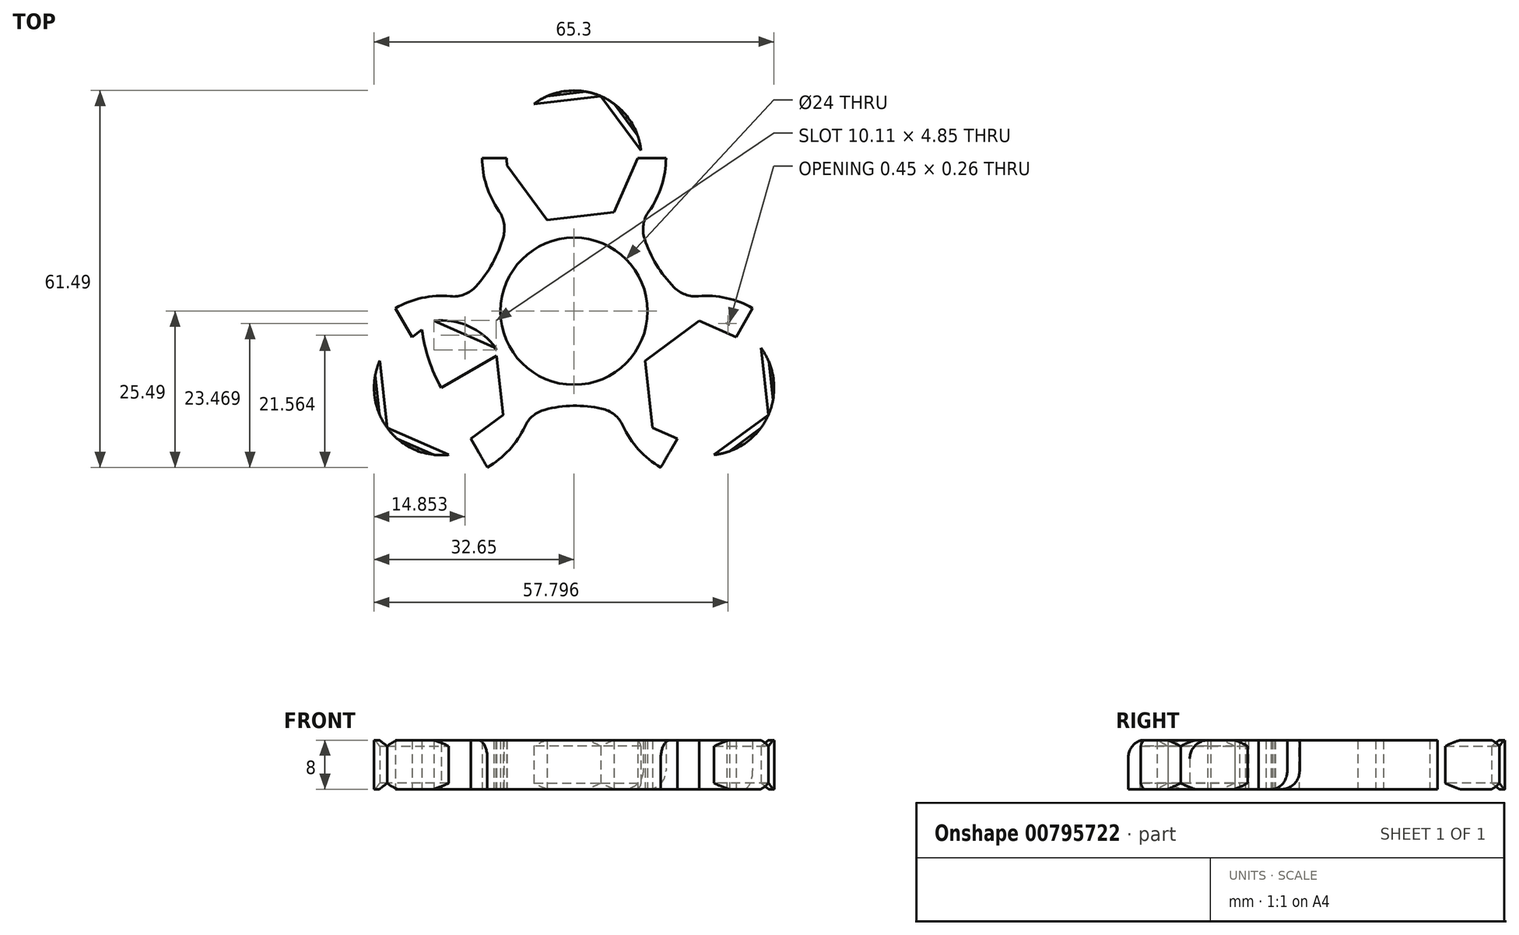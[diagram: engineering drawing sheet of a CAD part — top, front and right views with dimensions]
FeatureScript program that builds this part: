
annotation { "Feature Type Name" : "Feature", "Feature Type Description" : "" }
export const myFeature = defineFeature(function(context is Context, id is Id, definition is map)
    precondition{}
    {
        {
            var Q0;
            Q0=qCreatedBy(makeId("Top.planeOp"),FACE);
            var sketch = newSketch(context, id + "F0", { "sketchPlane" : qUnion([Q0])});
            skCircle(sketch, "E0.cCircle", {"center": v(0, 0) * mm, "radius": 25 * mm, "construction": true});
            skLineSegment(sketch, "E0.0", {"start": v(-43.3, 25) * mm, "end": v(43.3, 25) * mm});
            skLineSegment(sketch, "E0.1", {"start": v(43.3, 25) * mm, "end": v(0, -50) * mm});
            skLineSegment(sketch, "E0.2", {"start": v(-10.83, -31.25) * mm, "end": v(-43.3, 25) * mm});
            skPoint(sketch, "E0.0.midPoint", {"position": v(0, 25) * mm});
            skCircle(sketch, "E1", {"center": v(0, 0) * mm, "radius": 25 * mm});
            skLineSegment(sketch, "E2", {"start": v(0, 0) * mm, "end": v(-21.65, -12.5) * mm});
            skLineSegment(sketch, "E3", {"start": v(0, 0) * mm, "end": v(0, 25) * mm});
            skLineSegment(sketch, "E4", {"start": v(0, 0) * mm, "end": v(21.65, -12.5) * mm});
            skLineSegment(sketch, "E5", {"start": v(21.65, -12.5) * mm, "end": v(43.3, 25) * mm});
            skLineSegment(sketch, "E6", {"start": v(0, 25) * mm, "end": v(-43.3, 25) * mm});
            skLineSegment(sketch, "E7", {"start": v(-21.65, -12.5) * mm, "end": v(-43.3, 25) * mm});
            skLineSegment(sketch, "E8", {"start": v(-21.65, -12.5) * mm, "end": v(0, -50) * mm});
            skLineSegment(sketch, "E9", {"start": v(0, -50) * mm, "end": v(21.65, -12.5) * mm});
            skLineSegment(sketch, "E10", {"start": v(0, 25) * mm, "end": v(43.3, 25) * mm});
            skLineSegment(sketch, "E11", {"start": v(0, 25) * mm, "end": v(21.65, 25) * mm});
            skLineSegment(sketch, "E12", {"start": v(0, 25) * mm, "end": v(-21.65, 25) * mm});
            skLineSegment(sketch, "E13", {"start": v(-32.48, 6.25) * mm, "end": v(-43.3, 25) * mm});
            skLineSegment(sketch, "E14", {"start": v(-10.83, -31.25) * mm, "end": v(-21.65, -12.5) * mm});
            skLineSegment(sketch, "E15", {"start": v(21.65, -12.5) * mm, "end": v(32.48, 6.25) * mm});
            skLineSegment(sketch, "E16", {"start": v(32.48, 6.25) * mm, "end": v(27.06, -3.12) * mm});
            skLineSegment(sketch, "E17", {"start": v(21.65, 25) * mm, "end": v(10.83, 25) * mm});
            skLineSegment(sketch, "E18", {"start": v(-21.65, -12.5) * mm, "end": v(-16.24, -21.87) * mm});
            skArc(sketch, "E19", {"start": v(-16.24, -21.88) * mm, "mid": v(-12.28, -7.09) * mm, "end": v(-27.06, -3.12) * mm});
            skLineSegment(sketch, "E20", {"start": v(-16.24, -21.87) * mm, "end": v(-14.1, -20.64) * mm});
            skLineSegment(sketch, "E21", {"start": v(16.24, -21.87) * mm, "end": v(0, -12.5) * mm});
            skLineSegment(sketch, "E22", {"start": v(-16.24, -21.88) * mm, "end": v(0, -12.5) * mm});
            skLineSegment(sketch, "E23", {"start": v(-27.06, -3.12) * mm, "end": v(-10.83, 6.25) * mm});
            skLineSegment(sketch, "E24", {"start": v(-10.83, 25) * mm, "end": v(-10.83, 6.25) * mm});
            skLineSegment(sketch, "E25", {"start": v(10.83, 25) * mm, "end": v(10.83, 6.25) * mm});
            skLineSegment(sketch, "E26", {"start": v(27.06, -3.12) * mm, "end": v(10.83, 6.25) * mm});
            skCircle(sketch, "E27", {"center": v(-21.65, -12.5) * mm, "radius": 15 * mm});
            skCircle(sketch, "E28", {"center": v(0, 25) * mm, "radius": 15 * mm});
            skCircle(sketch, "E29", {"center": v(21.65, -12.5) * mm, "radius": 15 * mm});
            skCircle(sketch, "E30", {"center": v(0, 0) * mm, "radius": 12 * mm});
            skCircle(sketch, "E31", {"center": v(0, 25) * mm, "radius": 11 * mm});
            skCircle(sketch, "E32", {"center": v(-21.65, -12.5) * mm, "radius": 11 * mm});
            skCircle(sketch, "E33", {"center": v(21.65, -12.5) * mm, "radius": 11 * mm});
            skCircle(sketch, "E34.cCircle", {"center": v(21.65, -12.5) * mm, "radius": 11 * mm, "construction": true});
            skLineSegment(sketch, "E34.0", {"start": v(22.85, -23.43) * mm, "end": v(12.78, -19) * mm});
            skLineSegment(sketch, "E34.1", {"start": v(12.78, -19) * mm, "end": v(11.58, -8.07) * mm});
            skLineSegment(sketch, "E34.2", {"start": v(11.58, -8.07) * mm, "end": v(20.45, -1.57) * mm});
            skLineSegment(sketch, "E34.3", {"start": v(20.45, -1.57) * mm, "end": v(30.52, -6) * mm});
            skLineSegment(sketch, "E34.4", {"start": v(30.52, -6) * mm, "end": v(31.72, -16.93) * mm});
            skLineSegment(sketch, "E34.5", {"start": v(31.72, -16.93) * mm, "end": v(22.85, -23.43) * mm});
            skCircle(sketch, "E35.cCircle", {"center": v(-21.65, -12.5) * mm, "radius": 11 * mm, "construction": true});
            skLineSegment(sketch, "E35.0", {"start": v(-20.45, -23.43) * mm, "end": v(-30.52, -19) * mm});
            skLineSegment(sketch, "E35.1", {"start": v(-30.52, -19) * mm, "end": v(-31.72, -8.07) * mm});
            skLineSegment(sketch, "E35.2", {"start": v(-31.72, -8.07) * mm, "end": v(-22.85, -1.57) * mm});
            skLineSegment(sketch, "E35.3", {"start": v(-22.85, -1.57) * mm, "end": v(-12.78, -6) * mm});
            skLineSegment(sketch, "E35.4", {"start": v(-12.78, -6) * mm, "end": v(-11.58, -16.93) * mm});
            skLineSegment(sketch, "E35.5", {"start": v(-11.58, -16.93) * mm, "end": v(-20.45, -23.43) * mm});
            skCircle(sketch, "E36.cCircle", {"center": v(0, 25) * mm, "radius": 11 * mm, "construction": true});
            skLineSegment(sketch, "E36.0", {"start": v(-4.38, 14.9) * mm, "end": v(-10.93, 23.75) * mm});
            skLineSegment(sketch, "E36.1", {"start": v(-10.93, 23.75) * mm, "end": v(-6.55, 33.84) * mm});
            skLineSegment(sketch, "E36.2", {"start": v(-6.55, 33.84) * mm, "end": v(4.38, 35.1) * mm});
            skLineSegment(sketch, "E36.3", {"start": v(4.38, 35.1) * mm, "end": v(10.93, 26.25) * mm});
            skLineSegment(sketch, "E36.4", {"start": v(10.93, 26.25) * mm, "end": v(6.55, 16.16) * mm});
            skLineSegment(sketch, "E36.5", {"start": v(6.55, 16.16) * mm, "end": v(-4.38, 14.9) * mm});
            skSolve(sketch);
        }
        {
            var Q0;
            {var subQ0=sQuery(id+"F0.wireOp",EDGE,"E29");var subQ1=sQuery(id+"F0.wireOp",EDGE,"E9");var subQ2=makeQuery(id+"F0.imprint","INTERSECT",VERTEX,{"derivedFrom":[subQ1,subQ0]});Q0=makeQuery(id+"F0.imprint","IMPRINT",FACE,{"disambiguationData":[TD([[makeQuery(id+"F0.imprint","IMPRINT",EDGE,{"disambiguationData":[TD([[subQ2,-1.0]])],"derivedFrom":subQ1}),-1.0]])]});}
            var Q1;
            {var subQ0=sQuery(id+"F0.wireOp",EDGE,"E34.4");Q1=makeQuery(id+"F0.imprint","IMPRINT",FACE,{"disambiguationData":[TD([[makeQuery(id+"F0.imprint","IMPRINT",EDGE,{"derivedFrom":subQ0}),1.0]])]});}
            var Q2;
            {var subQ0=sQuery(id+"F0.wireOp",EDGE,"E34.5");Q2=makeQuery(id+"F0.imprint","IMPRINT",FACE,{"disambiguationData":[TD([[makeQuery(id+"F0.imprint","IMPRINT",EDGE,{"derivedFrom":subQ0}),1.0]])]});}
            var Q3;
            {var subQ0=sQuery(id+"F0.wireOp",EDGE,"E9");var subQ1=makeQuery(id+"F0.imprint","INTERSECT",VERTEX,{"derivedFrom":[subQ0,sQuery(id+"F0.wireOp",EDGE,"E21")]});Q3=makeQuery(id+"F0.imprint","IMPRINT",FACE,{"disambiguationData":[TD([[makeQuery(id+"F0.imprint","IMPRINT",EDGE,{"disambiguationData":[TD([[subQ1,1.0]])],"derivedFrom":subQ0}),-1.0]])]});}
            var Q4;
            {var subQ3=sQuery(id+"F0.wireOp",EDGE,"E33");var subQ5=sQuery(id+"F0.wireOp",EDGE,"E1");var subQ6=makeQuery(id+"F0.imprint","INTERSECT",VERTEX,{"disambiguationData":[OD(0.0)],"derivedFrom":[subQ5,subQ3]});Q4=makeQuery(id+"F0.imprint","IMPRINT",FACE,{"disambiguationData":[TD([[makeQuery(id+"F0.imprint","IMPRINT",EDGE,{"disambiguationData":[TD([[subQ6,-1.0]])],"derivedFrom":subQ5}),-1.0]])]});}
            var Q5;
            {var subQ0=sQuery(id+"F0.wireOp",EDGE,"E21");var subQ1=sQuery(id+"F0.wireOp",EDGE,"E9");var subQ2=makeQuery(id+"F0.imprint","INTERSECT",VERTEX,{"derivedFrom":[subQ1,subQ0]});Q5=makeQuery(id+"F0.imprint","IMPRINT",FACE,{"disambiguationData":[TD([[makeQuery(id+"F0.imprint","IMPRINT",EDGE,{"disambiguationData":[TD([[subQ2,1.0]])],"derivedFrom":subQ1}),1.0]])]});}
            var Q6;
            {var subQ0=sQuery(id+"F0.wireOp",EDGE,"E33");var subQ1=sQuery(id+"F0.wireOp",EDGE,"E1");var subQ2=makeQuery(id+"F0.imprint","INTERSECT",VERTEX,{"disambiguationData":[OD(0.0)],"derivedFrom":[subQ1,subQ0]});Q6=makeQuery(id+"F0.imprint","IMPRINT",FACE,{"disambiguationData":[TD([[makeQuery(id+"F0.imprint","IMPRINT",EDGE,{"disambiguationData":[TD([[subQ2,-1.0]])],"derivedFrom":subQ1}),1.0]])]});}
            var Q7;
            {var subQ0=sQuery(id+"F0.wireOp",EDGE,"E21");var subQ1=sQuery(id+"F0.wireOp",EDGE,"E1");var subQ2=makeQuery(id+"F0.imprint","INTERSECT",VERTEX,{"derivedFrom":[subQ1,subQ0]});Q7=makeQuery(id+"F0.imprint","IMPRINT",FACE,{"disambiguationData":[TD([[makeQuery(id+"F0.imprint","IMPRINT",EDGE,{"disambiguationData":[TD([[subQ2,-1.0]])],"derivedFrom":subQ1}),-1.0]])]});}
            var Q8;
            {var subQ0=sQuery(id+"F0.wireOp",EDGE,"E29");var subQ5=sQuery(id+"F0.wireOp",EDGE,"E1");var subQ6=makeQuery(id+"F0.imprint","INTERSECT",VERTEX,{"disambiguationData":[OD(1.0)],"derivedFrom":[subQ5,subQ0]});Q8=makeQuery(id+"F0.imprint","IMPRINT",FACE,{"disambiguationData":[TD([[makeQuery(id+"F0.imprint","IMPRINT",EDGE,{"disambiguationData":[TD([[subQ6,-1.0]])],"derivedFrom":subQ5}),-1.0]])]});}
            var Q9;
            {var subQ0=sQuery(id+"F0.wireOp",EDGE,"E29");var subQ1=sQuery(id+"F0.wireOp",EDGE,"E1");var subQ2=makeQuery(id+"F0.imprint","INTERSECT",VERTEX,{"disambiguationData":[OD(1.0)],"derivedFrom":[subQ1,subQ0]});Q9=makeQuery(id+"F0.imprint","IMPRINT",FACE,{"disambiguationData":[TD([[makeQuery(id+"F0.imprint","IMPRINT",EDGE,{"disambiguationData":[TD([[subQ2,-1.0]])],"derivedFrom":subQ1}),1.0]])]});}
            var Q10;
            {var subQ1=sQuery(id+"F0.wireOp",EDGE,"E21");var subQ10=sQuery(id+"F0.wireOp",EDGE,"E1");var subQ11=makeQuery(id+"F0.imprint","INTERSECT",VERTEX,{"derivedFrom":[subQ10,subQ1]});Q10=makeQuery(id+"F0.imprint","IMPRINT",FACE,{"disambiguationData":[TD([[makeQuery(id+"F0.imprint","IMPRINT",EDGE,{"disambiguationData":[TD([[subQ11,-1.0]])],"derivedFrom":subQ10}),1.0]])]});}
            var Q11;
            {var subQ0=sQuery(id+"F0.wireOp",EDGE,"E34.1");Q11=makeQuery(id+"F0.imprint","IMPRINT",FACE,{"disambiguationData":[TD([[makeQuery(id+"F0.imprint","IMPRINT",EDGE,{"derivedFrom":subQ0}),1.0]])]});}
            var Q12;
            {var subQ0=sQuery(id+"F0.wireOp",EDGE,"E33");var subQ1=sQuery(id+"F0.wireOp",EDGE,"E4");var subQ2=makeQuery(id+"F0.imprint","INTERSECT",VERTEX,{"derivedFrom":[subQ1,subQ0]});Q12=makeQuery(id+"F0.imprint","IMPRINT",FACE,{"disambiguationData":[TD([[makeQuery(id+"F0.imprint","IMPRINT",EDGE,{"disambiguationData":[TD([[subQ2,-1.0]])],"derivedFrom":subQ1}),1.0]])]});}
            var Q13;
            {var subQ0=sQuery(id+"F0.wireOp",EDGE,"E33");var subQ1=sQuery(id+"F0.wireOp",EDGE,"E4");var subQ2=makeQuery(id+"F0.imprint","INTERSECT",VERTEX,{"derivedFrom":[subQ1,subQ0]});Q13=makeQuery(id+"F0.imprint","IMPRINT",FACE,{"disambiguationData":[TD([[makeQuery(id+"F0.imprint","IMPRINT",EDGE,{"disambiguationData":[TD([[subQ2,-1.0]])],"derivedFrom":subQ1}),-1.0]])]});}
            var Q14;
            {var subQ0=sQuery(id+"F0.wireOp",EDGE,"E34.3");var subQ1=sQuery(id+"F0.wireOp",EDGE,"E1");var subQ2=makeQuery(id+"F0.imprint","INTERSECT",VERTEX,{"derivedFrom":[subQ1,subQ0]});Q14=makeQuery(id+"F0.imprint","IMPRINT",FACE,{"disambiguationData":[TD([[makeQuery(id+"F0.imprint","IMPRINT",EDGE,{"disambiguationData":[TD([[subQ2,-1.0]])],"derivedFrom":subQ1}),1.0]])]});}
            var Q15;
            {var subQ1=sQuery(id+"F0.wireOp",EDGE,"E1");var subQ5=sQuery(id+"F0.wireOp",EDGE,"E34.3");var subQ6=makeQuery(id+"F0.imprint","INTERSECT",VERTEX,{"derivedFrom":[subQ1,subQ5]});Q15=makeQuery(id+"F0.imprint","IMPRINT",FACE,{"disambiguationData":[TD([[makeQuery(id+"F0.imprint","IMPRINT",EDGE,{"disambiguationData":[TD([[subQ6,-1.0]])],"derivedFrom":subQ1}),-1.0]])]});}
            var Q16;
            {var subQ1=sQuery(id+"F0.wireOp",EDGE,"E15");var subQ3=sQuery(id+"F0.wireOp",EDGE,"E34.3");var subQ4=makeQuery(id+"F0.imprint","INTERSECT",VERTEX,{"derivedFrom":[subQ1,subQ3]});Q16=makeQuery(id+"F0.imprint","IMPRINT",FACE,{"disambiguationData":[TD([[makeQuery(id+"F0.imprint","IMPRINT",EDGE,{"disambiguationData":[TD([[subQ4,-1.0]])],"derivedFrom":subQ1}),-1.0]])]});}
            var Q17;
            {var subQ1=sQuery(id+"F0.wireOp",EDGE,"E16");var subQ3=sQuery(id+"F0.wireOp",EDGE,"E33");var subQ4=makeQuery(id+"F0.imprint","INTERSECT",VERTEX,{"derivedFrom":[subQ1,subQ3]});Q17=makeQuery(id+"F0.imprint","IMPRINT",FACE,{"disambiguationData":[TD([[makeQuery(id+"F0.imprint","IMPRINT",EDGE,{"disambiguationData":[TD([[subQ4,-1.0]])],"derivedFrom":subQ3}),1.0]])]});}
            var Q18;
            {var subQ0=sQuery(id+"F0.wireOp",EDGE,"E29");var subQ3=sQuery(id+"F0.wireOp",EDGE,"E1");var subQ4=makeQuery(id+"F0.imprint","INTERSECT",VERTEX,{"disambiguationData":[OD(0.0)],"derivedFrom":[subQ3,subQ0]});Q18=makeQuery(id+"F0.imprint","IMPRINT",FACE,{"disambiguationData":[TD([[makeQuery(id+"F0.imprint","IMPRINT",EDGE,{"disambiguationData":[TD([[subQ4,1.0]])],"derivedFrom":subQ3}),-1.0]])]});}
            var Q19;
            {var subQ5=sQuery(id+"F0.wireOp",EDGE,"E1");var subQ9=sQuery(id+"F0.wireOp",EDGE,"E33");var subQ11=makeQuery(id+"F0.imprint","INTERSECT",VERTEX,{"disambiguationData":[OD(1.0)],"derivedFrom":[subQ5,subQ9]});Q19=makeQuery(id+"F0.imprint","IMPRINT",FACE,{"disambiguationData":[TD([[makeQuery(id+"F0.imprint","IMPRINT",EDGE,{"disambiguationData":[TD([[subQ11,-1.0]])],"derivedFrom":subQ5}),1.0]])]});}
            var Q20;
            {var subQ0=sQuery(id+"F0.wireOp",EDGE,"E29");var subQ1=sQuery(id+"F0.wireOp",EDGE,"E1");var subQ2=makeQuery(id+"F0.imprint","INTERSECT",VERTEX,{"disambiguationData":[OD(0.0)],"derivedFrom":[subQ1,subQ0]});Q20=makeQuery(id+"F0.imprint","IMPRINT",FACE,{"disambiguationData":[TD([[makeQuery(id+"F0.imprint","IMPRINT",EDGE,{"disambiguationData":[TD([[subQ2,1.0]])],"derivedFrom":subQ1}),1.0]])]});}
            var Q21;
            {var subQ1=sQuery(id+"F0.wireOp",EDGE,"E21");var subQ6=sQuery(id+"F0.wireOp",EDGE,"E22");var subQ9=makeQuery(id+"F0.imprint","INTERSECT",VERTEX,{"derivedFrom":[subQ1,subQ6]});Q21=makeQuery(id+"F0.imprint","IMPRINT",FACE,{"disambiguationData":[TD([[makeQuery(id+"F0.imprint","IMPRINT",EDGE,{"disambiguationData":[TD([[subQ9,1.0]])],"derivedFrom":subQ1}),-1.0]])]});}
            var Q22;
            {var subQ0=sQuery(id+"F0.wireOp",EDGE,"E22");var subQ1=sQuery(id+"F0.wireOp",EDGE,"E1");var subQ2=makeQuery(id+"F0.imprint","INTERSECT",VERTEX,{"derivedFrom":[subQ1,subQ0]});Q22=makeQuery(id+"F0.imprint","IMPRINT",FACE,{"disambiguationData":[TD([[makeQuery(id+"F0.imprint","IMPRINT",EDGE,{"disambiguationData":[TD([[subQ2,-1.0]])],"derivedFrom":subQ1}),1.0]])]});}
            var Q23;
            {var subQ3=sQuery(id+"F0.wireOp",EDGE,"E1");var subQ5=sQuery(id+"F0.wireOp",EDGE,"E22");var subQ6=makeQuery(id+"F0.imprint","INTERSECT",VERTEX,{"derivedFrom":[subQ3,subQ5]});Q23=makeQuery(id+"F0.imprint","IMPRINT",FACE,{"disambiguationData":[TD([[makeQuery(id+"F0.imprint","IMPRINT",EDGE,{"disambiguationData":[TD([[subQ6,-1.0]])],"derivedFrom":subQ3}),-1.0]])]});}
            var Q24;
            {var subQ0=sQuery(id+"F0.wireOp",EDGE,"E27");var subQ1=sQuery(id+"F0.wireOp",EDGE,"E7");var subQ2=makeQuery(id+"F0.imprint","INTERSECT",VERTEX,{"derivedFrom":[subQ1,subQ0]});Q24=makeQuery(id+"F0.imprint","IMPRINT",FACE,{"disambiguationData":[TD([[makeQuery(id+"F0.imprint","IMPRINT",EDGE,{"disambiguationData":[TD([[subQ2,1.0]])],"derivedFrom":subQ1}),1.0]])]});}
            var Q25;
            {var subQ1=sQuery(id+"F0.wireOp",EDGE,"E1");var subQ5=sQuery(id+"F0.wireOp",EDGE,"E27");var subQ8=makeQuery(id+"F0.imprint","INTERSECT",VERTEX,{"disambiguationData":[OD(0.0)],"derivedFrom":[subQ1,subQ5]});Q25=makeQuery(id+"F0.imprint","IMPRINT",FACE,{"disambiguationData":[TD([[makeQuery(id+"F0.imprint","IMPRINT",EDGE,{"disambiguationData":[TD([[subQ8,-1.0]])],"derivedFrom":subQ1}),-1.0]])]});}
            var Q26;
            {var subQ0=sQuery(id+"F0.wireOp",EDGE,"E27");var subQ1=sQuery(id+"F0.wireOp",EDGE,"E1");var subQ2=makeQuery(id+"F0.imprint","INTERSECT",VERTEX,{"disambiguationData":[OD(0.0)],"derivedFrom":[subQ1,subQ0]});Q26=makeQuery(id+"F0.imprint","IMPRINT",FACE,{"disambiguationData":[TD([[makeQuery(id+"F0.imprint","IMPRINT",EDGE,{"disambiguationData":[TD([[subQ2,-1.0]])],"derivedFrom":subQ1}),1.0]])]});}
            var Q27;
            {var subQ1=sQuery(id+"F0.wireOp",EDGE,"E23");var subQ5=sQuery(id+"F0.wireOp",EDGE,"E1");var subQ6=makeQuery(id+"F0.imprint","INTERSECT",VERTEX,{"derivedFrom":[subQ5,subQ1]});Q27=makeQuery(id+"F0.imprint","IMPRINT",FACE,{"disambiguationData":[TD([[makeQuery(id+"F0.imprint","IMPRINT",EDGE,{"disambiguationData":[TD([[subQ6,-1.0]])],"derivedFrom":subQ5}),1.0]])]});}
            var Q28;
            {var subQ5=sQuery(id+"F0.wireOp",EDGE,"E1");var subQ9=sQuery(id+"F0.wireOp",EDGE,"E32");var subQ11=makeQuery(id+"F0.imprint","INTERSECT",VERTEX,{"disambiguationData":[OD(1.0)],"derivedFrom":[subQ5,subQ9]});Q28=makeQuery(id+"F0.imprint","IMPRINT",FACE,{"disambiguationData":[TD([[makeQuery(id+"F0.imprint","IMPRINT",EDGE,{"disambiguationData":[TD([[subQ11,-1.0]])],"derivedFrom":subQ5}),1.0]])]});}
            var Q29;
            {var subQ1=sQuery(id+"F0.wireOp",EDGE,"E7");var subQ3=sQuery(id+"F0.wireOp",EDGE,"E32");var subQ4=makeQuery(id+"F0.imprint","INTERSECT",VERTEX,{"derivedFrom":[subQ1,subQ3]});Q29=makeQuery(id+"F0.imprint","IMPRINT",FACE,{"disambiguationData":[TD([[makeQuery(id+"F0.imprint","IMPRINT",EDGE,{"disambiguationData":[TD([[subQ4,1.0]])],"derivedFrom":subQ3}),1.0]])]});}
            var Q30;
            {var subQ0=sQuery(id+"F0.wireOp",EDGE,"E23");var subQ1=sQuery(id+"F0.wireOp",EDGE,"E1");var subQ2=makeQuery(id+"F0.imprint","INTERSECT",VERTEX,{"derivedFrom":[subQ1,subQ0]});Q30=makeQuery(id+"F0.imprint","IMPRINT",FACE,{"disambiguationData":[TD([[makeQuery(id+"F0.imprint","IMPRINT",EDGE,{"disambiguationData":[TD([[subQ2,-1.0]])],"derivedFrom":subQ1}),-1.0]])]});}
            var Q31;
            {var subQ0=sQuery(id+"F0.wireOp",EDGE,"E32");var subQ1=sQuery(id+"F0.wireOp",EDGE,"E1");var subQ2=makeQuery(id+"F0.imprint","INTERSECT",VERTEX,{"disambiguationData":[OD(0.0)],"derivedFrom":[subQ1,subQ0]});Q31=makeQuery(id+"F0.imprint","IMPRINT",FACE,{"disambiguationData":[TD([[makeQuery(id+"F0.imprint","IMPRINT",EDGE,{"disambiguationData":[TD([[subQ2,-1.0]])],"derivedFrom":subQ1}),-1.0]])]});}
            var Q32;
            {var subQ0=sQuery(id+"F0.wireOp",EDGE,"E32");var subQ1=sQuery(id+"F0.wireOp",EDGE,"E1");var subQ2=makeQuery(id+"F0.imprint","INTERSECT",VERTEX,{"disambiguationData":[OD(0.0)],"derivedFrom":[subQ1,subQ0]});Q32=makeQuery(id+"F0.imprint","IMPRINT",FACE,{"disambiguationData":[TD([[makeQuery(id+"F0.imprint","IMPRINT",EDGE,{"disambiguationData":[TD([[subQ2,-1.0]])],"derivedFrom":subQ1}),1.0]])]});}
            var Q33;
            {var subQ0=sQuery(id+"F0.wireOp",EDGE,"E35.3");var subQ1=sQuery(id+"F0.wireOp",EDGE,"E19");var subQ2=makeQuery(id+"F0.imprint","INTERSECT",VERTEX,{"disambiguationData":[OD(0.0)],"derivedFrom":[subQ1,subQ0]});Q33=makeQuery(id+"F0.imprint","IMPRINT",FACE,{"disambiguationData":[TD([[makeQuery(id+"F0.imprint","IMPRINT",EDGE,{"disambiguationData":[TD([[subQ2,-1.0]])],"derivedFrom":subQ1}),-1.0]])]});}
            var Q34;
            {var subQ0=sQuery(id+"F0.wireOp",EDGE,"E19");var subQ1=sQuery(id+"F0.wireOp",EDGE,"E1");var subQ2=makeQuery(id+"F0.imprint","INTERSECT",VERTEX,{"disambiguationData":[OD(0.0)],"derivedFrom":[subQ1,subQ0]});Q34=makeQuery(id+"F0.imprint","IMPRINT",FACE,{"disambiguationData":[TD([[makeQuery(id+"F0.imprint","IMPRINT",EDGE,{"disambiguationData":[TD([[subQ2,-1.0]])],"derivedFrom":subQ1}),-1.0]])]});}
            var Q35;
            {var subQ0=sQuery(id+"F0.wireOp",EDGE,"E19");var subQ1=sQuery(id+"F0.wireOp",EDGE,"E1");var subQ2=makeQuery(id+"F0.imprint","INTERSECT",VERTEX,{"disambiguationData":[OD(0.0)],"derivedFrom":[subQ1,subQ0]});Q35=makeQuery(id+"F0.imprint","IMPRINT",FACE,{"disambiguationData":[TD([[makeQuery(id+"F0.imprint","IMPRINT",EDGE,{"disambiguationData":[TD([[subQ2,-1.0]])],"derivedFrom":subQ1}),1.0]])]});}
            var Q36;
            {var subQ0=sQuery(id+"F0.wireOp",EDGE,"E7");var subQ2=sQuery(id+"F0.wireOp",EDGE,"E35.2");var subQ3=makeQuery(id+"F0.imprint","INTERSECT",VERTEX,{"derivedFrom":[subQ0,subQ2]});Q36=makeQuery(id+"F0.imprint","IMPRINT",FACE,{"disambiguationData":[TD([[makeQuery(id+"F0.imprint","IMPRINT",EDGE,{"disambiguationData":[TD([[subQ3,-1.0]])],"derivedFrom":subQ0}),1.0]])]});}
            var Q37;
            {var subQ0=sQuery(id+"F0.wireOp",EDGE,"E35.1");Q37=makeQuery(id+"F0.imprint","IMPRINT",FACE,{"disambiguationData":[TD([[makeQuery(id+"F0.imprint","IMPRINT",EDGE,{"derivedFrom":subQ0}),1.0]])]});}
            var Q38;
            {var subQ0=sQuery(id+"F0.wireOp",EDGE,"E35.0");Q38=makeQuery(id+"F0.imprint","IMPRINT",FACE,{"disambiguationData":[TD([[makeQuery(id+"F0.imprint","IMPRINT",EDGE,{"derivedFrom":subQ0}),1.0]])]});}
            var Q39;
            {var subQ1=sQuery(id+"F0.wireOp",EDGE,"E14");var subQ3=sQuery(id+"F0.wireOp",EDGE,"E32");var subQ4=makeQuery(id+"F0.imprint","INTERSECT",VERTEX,{"derivedFrom":[subQ1,subQ3]});Q39=makeQuery(id+"F0.imprint","IMPRINT",FACE,{"disambiguationData":[TD([[makeQuery(id+"F0.imprint","IMPRINT",EDGE,{"disambiguationData":[TD([[subQ4,1.0]])],"derivedFrom":subQ3}),1.0]])]});}
            var Q40;
            {var subQ0=sQuery(id+"F0.wireOp",EDGE,"E19");var subQ1=sQuery(id+"F0.wireOp",EDGE,"E1");var subQ2=makeQuery(id+"F0.imprint","INTERSECT",VERTEX,{"disambiguationData":[OD(1.0)],"derivedFrom":[subQ1,subQ0]});Q40=makeQuery(id+"F0.imprint","IMPRINT",FACE,{"disambiguationData":[TD([[makeQuery(id+"F0.imprint","IMPRINT",EDGE,{"disambiguationData":[TD([[subQ2,-1.0]])],"derivedFrom":subQ1}),-1.0]])]});}
            var Q41;
            {var subQ1=sQuery(id+"F0.wireOp",EDGE,"E14");var subQ3=sQuery(id+"F0.wireOp",EDGE,"E32");var subQ4=makeQuery(id+"F0.imprint","INTERSECT",VERTEX,{"derivedFrom":[subQ1,subQ3]});Q41=makeQuery(id+"F0.imprint","IMPRINT",FACE,{"disambiguationData":[TD([[makeQuery(id+"F0.imprint","IMPRINT",EDGE,{"disambiguationData":[TD([[subQ4,-1.0]])],"derivedFrom":subQ3}),1.0]])]});}
            var Q42;
            {var subQ0=sQuery(id+"F0.wireOp",EDGE,"E35.5");var subQ1=sQuery(id+"F0.wireOp",EDGE,"E1");var subQ2=makeQuery(id+"F0.imprint","INTERSECT",VERTEX,{"derivedFrom":[subQ1,subQ0]});Q42=makeQuery(id+"F0.imprint","IMPRINT",FACE,{"disambiguationData":[TD([[makeQuery(id+"F0.imprint","IMPRINT",EDGE,{"disambiguationData":[TD([[subQ2,-1.0]])],"derivedFrom":subQ1}),-1.0]])]});}
            var Q43;
            {var subQ0=sQuery(id+"F0.wireOp",EDGE,"E32");var subQ1=sQuery(id+"F0.wireOp",EDGE,"E1");var subQ2=makeQuery(id+"F0.imprint","INTERSECT",VERTEX,{"disambiguationData":[OD(1.0)],"derivedFrom":[subQ1,subQ0]});Q43=makeQuery(id+"F0.imprint","IMPRINT",FACE,{"disambiguationData":[TD([[makeQuery(id+"F0.imprint","IMPRINT",EDGE,{"disambiguationData":[TD([[subQ2,-1.0]])],"derivedFrom":subQ1}),-1.0]])]});}
            var Q44;
            {var subQ0=sQuery(id+"F0.wireOp",EDGE,"E19");var subQ1=sQuery(id+"F0.wireOp",EDGE,"E1");var subQ2=makeQuery(id+"F0.imprint","INTERSECT",VERTEX,{"disambiguationData":[OD(1.0)],"derivedFrom":[subQ1,subQ0]});Q44=makeQuery(id+"F0.imprint","IMPRINT",FACE,{"disambiguationData":[TD([[makeQuery(id+"F0.imprint","IMPRINT",EDGE,{"disambiguationData":[TD([[subQ2,-1.0]])],"derivedFrom":subQ1}),1.0]])]});}
            var Q45;
            {var subQ0=sQuery(id+"F0.wireOp",EDGE,"E35.5");var subQ1=sQuery(id+"F0.wireOp",EDGE,"E1");var subQ2=makeQuery(id+"F0.imprint","INTERSECT",VERTEX,{"derivedFrom":[subQ1,subQ0]});Q45=makeQuery(id+"F0.imprint","IMPRINT",FACE,{"disambiguationData":[TD([[makeQuery(id+"F0.imprint","IMPRINT",EDGE,{"disambiguationData":[TD([[subQ2,-1.0]])],"derivedFrom":subQ1}),1.0]])]});}
            var Q46;
            {var subQ0=sQuery(id+"F0.wireOp",EDGE,"E32");var subQ1=sQuery(id+"F0.wireOp",EDGE,"E2");var subQ2=makeQuery(id+"F0.imprint","INTERSECT",VERTEX,{"derivedFrom":[subQ1,subQ0]});Q46=makeQuery(id+"F0.imprint","IMPRINT",FACE,{"disambiguationData":[TD([[makeQuery(id+"F0.imprint","IMPRINT",EDGE,{"disambiguationData":[TD([[subQ2,-1.0]])],"derivedFrom":subQ1}),1.0]])]});}
            var Q47;
            {var subQ0=sQuery(id+"F0.wireOp",EDGE,"E19");var subQ1=sQuery(id+"F0.wireOp",EDGE,"E2");var subQ2=makeQuery(id+"F0.imprint","INTERSECT",VERTEX,{"derivedFrom":[subQ1,subQ0]});Q47=makeQuery(id+"F0.imprint","IMPRINT",FACE,{"disambiguationData":[TD([[makeQuery(id+"F0.imprint","IMPRINT",EDGE,{"disambiguationData":[TD([[subQ2,-1.0]])],"derivedFrom":subQ1}),1.0]])]});}
            var Q48;
            {var subQ0=sQuery(id+"F0.wireOp",EDGE,"E19");var subQ1=sQuery(id+"F0.wireOp",EDGE,"E2");var subQ2=makeQuery(id+"F0.imprint","INTERSECT",VERTEX,{"derivedFrom":[subQ1,subQ0]});Q48=makeQuery(id+"F0.imprint","IMPRINT",FACE,{"disambiguationData":[TD([[makeQuery(id+"F0.imprint","IMPRINT",EDGE,{"disambiguationData":[TD([[subQ2,-1.0]])],"derivedFrom":subQ1}),-1.0]])]});}
            var Q49;
            {var subQ0=sQuery(id+"F0.wireOp",EDGE,"E32");var subQ1=sQuery(id+"F0.wireOp",EDGE,"E2");var subQ2=makeQuery(id+"F0.imprint","INTERSECT",VERTEX,{"derivedFrom":[subQ1,subQ0]});Q49=makeQuery(id+"F0.imprint","IMPRINT",FACE,{"disambiguationData":[TD([[makeQuery(id+"F0.imprint","IMPRINT",EDGE,{"disambiguationData":[TD([[subQ2,-1.0]])],"derivedFrom":subQ1}),-1.0]])]});}
            var Q50;
            {var subQ0=sQuery(id+"F0.wireOp",EDGE,"E35.3");var subQ1=sQuery(id+"F0.wireOp",EDGE,"E19");var subQ2=makeQuery(id+"F0.imprint","INTERSECT",VERTEX,{"disambiguationData":[OD(0.0)],"derivedFrom":[subQ1,subQ0]});Q50=makeQuery(id+"F0.imprint","IMPRINT",FACE,{"disambiguationData":[TD([[makeQuery(id+"F0.imprint","IMPRINT",EDGE,{"disambiguationData":[TD([[subQ2,-1.0]])],"derivedFrom":subQ1}),1.0]])]});}
            var Q51;
            {var subQ1=sQuery(id+"F0.wireOp",EDGE,"E24");var subQ6=sQuery(id+"F0.wireOp",EDGE,"E23");var subQ9=makeQuery(id+"F0.imprint","INTERSECT",VERTEX,{"derivedFrom":[subQ6,subQ1]});Q51=makeQuery(id+"F0.imprint","IMPRINT",FACE,{"disambiguationData":[TD([[makeQuery(id+"F0.imprint","IMPRINT",EDGE,{"disambiguationData":[TD([[subQ9,1.0]])],"derivedFrom":subQ6}),-1.0]])]});}
            var Q52;
            {var subQ0=sQuery(id+"F0.wireOp",EDGE,"E24");var subQ1=sQuery(id+"F0.wireOp",EDGE,"E1");var subQ2=makeQuery(id+"F0.imprint","INTERSECT",VERTEX,{"derivedFrom":[subQ1,subQ0]});Q52=makeQuery(id+"F0.imprint","IMPRINT",FACE,{"disambiguationData":[TD([[makeQuery(id+"F0.imprint","IMPRINT",EDGE,{"disambiguationData":[TD([[subQ2,-1.0]])],"derivedFrom":subQ1}),1.0]])]});}
            var Q53;
            {var subQ5=sQuery(id+"F0.wireOp",EDGE,"E28");var subQ6=sQuery(id+"F0.wireOp",EDGE,"E12");var subQ7=makeQuery(id+"F0.imprint","INTERSECT",VERTEX,{"derivedFrom":[subQ6,subQ5]});Q53=makeQuery(id+"F0.imprint","IMPRINT",FACE,{"disambiguationData":[TD([[makeQuery(id+"F0.imprint","IMPRINT",EDGE,{"disambiguationData":[TD([[subQ7,1.0]])],"derivedFrom":subQ6}),-1.0]])]});}
            var Q54;
            {var subQ0=sQuery(id+"F0.wireOp",EDGE,"E28");var subQ3=sQuery(id+"F0.wireOp",EDGE,"E1");var subQ4=makeQuery(id+"F0.imprint","INTERSECT",VERTEX,{"disambiguationData":[OD(0.0)],"derivedFrom":[subQ3,subQ0]});Q54=makeQuery(id+"F0.imprint","IMPRINT",FACE,{"disambiguationData":[TD([[makeQuery(id+"F0.imprint","IMPRINT",EDGE,{"disambiguationData":[TD([[subQ4,-1.0]])],"derivedFrom":subQ3}),-1.0]])]});}
            var Q55;
            {var subQ0=sQuery(id+"F0.wireOp",EDGE,"E28");var subQ1=sQuery(id+"F0.wireOp",EDGE,"E1");var subQ2=makeQuery(id+"F0.imprint","INTERSECT",VERTEX,{"disambiguationData":[OD(0.0)],"derivedFrom":[subQ1,subQ0]});Q55=makeQuery(id+"F0.imprint","IMPRINT",FACE,{"disambiguationData":[TD([[makeQuery(id+"F0.imprint","IMPRINT",EDGE,{"disambiguationData":[TD([[subQ2,-1.0]])],"derivedFrom":subQ1}),1.0]])]});}
            var Q56;
            {var subQ5=sQuery(id+"F0.wireOp",EDGE,"E1");var subQ7=sQuery(id+"F0.wireOp",EDGE,"E31");var subQ8=makeQuery(id+"F0.imprint","INTERSECT",VERTEX,{"disambiguationData":[OD(1.0)],"derivedFrom":[subQ5,subQ7]});Q56=makeQuery(id+"F0.imprint","IMPRINT",FACE,{"disambiguationData":[TD([[makeQuery(id+"F0.imprint","IMPRINT",EDGE,{"disambiguationData":[TD([[subQ8,-1.0]])],"derivedFrom":subQ5}),1.0]])]});}
            var Q57;
            {var subQ3=sQuery(id+"F0.wireOp",EDGE,"E1");var subQ5=sQuery(id+"F0.wireOp",EDGE,"E24");var subQ6=makeQuery(id+"F0.imprint","INTERSECT",VERTEX,{"derivedFrom":[subQ3,subQ5]});Q57=makeQuery(id+"F0.imprint","IMPRINT",FACE,{"disambiguationData":[TD([[makeQuery(id+"F0.imprint","IMPRINT",EDGE,{"disambiguationData":[TD([[subQ6,-1.0]])],"derivedFrom":subQ3}),-1.0]])]});}
            var Q58;
            {var subQ1=sQuery(id+"F0.wireOp",EDGE,"E25");var subQ5=sQuery(id+"F0.wireOp",EDGE,"E1");var subQ6=makeQuery(id+"F0.imprint","INTERSECT",VERTEX,{"derivedFrom":[subQ5,subQ1]});Q58=makeQuery(id+"F0.imprint","IMPRINT",FACE,{"disambiguationData":[TD([[makeQuery(id+"F0.imprint","IMPRINT",EDGE,{"disambiguationData":[TD([[subQ6,-1.0]])],"derivedFrom":subQ5}),1.0]])]});}
            var Q59;
            {var subQ0=sQuery(id+"F0.wireOp",EDGE,"E31");var subQ1=sQuery(id+"F0.wireOp",EDGE,"E1");var subQ2=makeQuery(id+"F0.imprint","INTERSECT",VERTEX,{"disambiguationData":[OD(0.0)],"derivedFrom":[subQ1,subQ0]});Q59=makeQuery(id+"F0.imprint","IMPRINT",FACE,{"disambiguationData":[TD([[makeQuery(id+"F0.imprint","IMPRINT",EDGE,{"disambiguationData":[TD([[subQ2,-1.0]])],"derivedFrom":subQ1}),1.0]])]});}
            var Q60;
            {var subQ0=sQuery(id+"F0.wireOp",EDGE,"E31");var subQ1=sQuery(id+"F0.wireOp",EDGE,"E3");var subQ2=makeQuery(id+"F0.imprint","INTERSECT",VERTEX,{"derivedFrom":[subQ1,subQ0]});Q60=makeQuery(id+"F0.imprint","IMPRINT",FACE,{"disambiguationData":[TD([[makeQuery(id+"F0.imprint","IMPRINT",EDGE,{"disambiguationData":[TD([[subQ2,-1.0]])],"derivedFrom":subQ1}),-1.0]])]});}
            var Q61;
            {var subQ0=sQuery(id+"F0.wireOp",EDGE,"E31");var subQ1=sQuery(id+"F0.wireOp",EDGE,"E3");var subQ2=makeQuery(id+"F0.imprint","INTERSECT",VERTEX,{"derivedFrom":[subQ1,subQ0]});Q61=makeQuery(id+"F0.imprint","IMPRINT",FACE,{"disambiguationData":[TD([[makeQuery(id+"F0.imprint","IMPRINT",EDGE,{"disambiguationData":[TD([[subQ2,-1.0]])],"derivedFrom":subQ1}),1.0]])]});}
            var Q62;
            {var subQ0=sQuery(id+"F0.wireOp",EDGE,"E36.0");var subQ1=sQuery(id+"F0.wireOp",EDGE,"E1");var subQ2=makeQuery(id+"F0.imprint","INTERSECT",VERTEX,{"derivedFrom":[subQ1,subQ0]});Q62=makeQuery(id+"F0.imprint","IMPRINT",FACE,{"disambiguationData":[TD([[makeQuery(id+"F0.imprint","IMPRINT",EDGE,{"disambiguationData":[TD([[subQ2,-1.0]])],"derivedFrom":subQ1}),1.0]])]});}
            var Q63;
            {var subQ0=sQuery(id+"F0.wireOp",EDGE,"E12");var subQ1=makeQuery(id+"F0.imprint","INTERSECT",VERTEX,{"derivedFrom":[subQ0,sQuery(id+"F0.wireOp",EDGE,"E24")]});Q63=makeQuery(id+"F0.imprint","IMPRINT",FACE,{"disambiguationData":[TD([[makeQuery(id+"F0.imprint","IMPRINT",EDGE,{"disambiguationData":[TD([[subQ1,1.0]])],"derivedFrom":subQ0}),-1.0]])]});}
            var Q64;
            {var subQ0=sQuery(id+"F0.wireOp",EDGE,"E36.0");var subQ1=sQuery(id+"F0.wireOp",EDGE,"E1");var subQ2=makeQuery(id+"F0.imprint","INTERSECT",VERTEX,{"derivedFrom":[subQ1,subQ0]});Q64=makeQuery(id+"F0.imprint","IMPRINT",FACE,{"disambiguationData":[TD([[makeQuery(id+"F0.imprint","IMPRINT",EDGE,{"disambiguationData":[TD([[subQ2,-1.0]])],"derivedFrom":subQ1}),-1.0]])]});}
            var Q65;
            {var subQ0=sQuery(id+"F0.wireOp",EDGE,"E31");var subQ1=sQuery(id+"F0.wireOp",EDGE,"E1");var subQ2=makeQuery(id+"F0.imprint","INTERSECT",VERTEX,{"disambiguationData":[OD(1.0)],"derivedFrom":[subQ1,subQ0]});Q65=makeQuery(id+"F0.imprint","IMPRINT",FACE,{"disambiguationData":[TD([[makeQuery(id+"F0.imprint","IMPRINT",EDGE,{"disambiguationData":[TD([[subQ2,-1.0]])],"derivedFrom":subQ1}),-1.0]])]});}
            var Q66;
            {var subQ0=sQuery(id+"F0.wireOp",EDGE,"E36.0");var subQ1=sQuery(id+"F0.wireOp",EDGE,"E24");var subQ2=makeQuery(id+"F0.imprint","INTERSECT",VERTEX,{"derivedFrom":[subQ1,subQ0]});Q66=makeQuery(id+"F0.imprint","IMPRINT",FACE,{"disambiguationData":[TD([[makeQuery(id+"F0.imprint","IMPRINT",EDGE,{"disambiguationData":[TD([[subQ2,-1.0]])],"derivedFrom":subQ1}),-1.0]])]});}
            var Q67;
            {var subQ0=sQuery(id+"F0.wireOp",EDGE,"E24");var subQ1=sQuery(id+"F0.wireOp",EDGE,"E12");var subQ2=makeQuery(id+"F0.imprint","INTERSECT",VERTEX,{"derivedFrom":[subQ1,subQ0]});Q67=makeQuery(id+"F0.imprint","IMPRINT",FACE,{"disambiguationData":[TD([[makeQuery(id+"F0.imprint","IMPRINT",EDGE,{"disambiguationData":[TD([[subQ2,-1.0]])],"derivedFrom":subQ1}),1.0]])]});}
            var Q68;
            {var subQ0=sQuery(id+"F0.wireOp",EDGE,"E24");var subQ1=sQuery(id+"F0.wireOp",EDGE,"E12");var subQ2=makeQuery(id+"F0.imprint","INTERSECT",VERTEX,{"derivedFrom":[subQ1,subQ0]});Q68=makeQuery(id+"F0.imprint","IMPRINT",FACE,{"disambiguationData":[TD([[makeQuery(id+"F0.imprint","IMPRINT",EDGE,{"disambiguationData":[TD([[subQ2,1.0]])],"derivedFrom":subQ1}),1.0]])]});}
            var Q69;
            {var subQ0=sQuery(id+"F0.wireOp",EDGE,"E36.2");Q69=makeQuery(id+"F0.imprint","IMPRINT",FACE,{"disambiguationData":[TD([[makeQuery(id+"F0.imprint","IMPRINT",EDGE,{"derivedFrom":subQ0}),1.0]])]});}
            var Q70;
            {var subQ0=sQuery(id+"F0.wireOp",EDGE,"E36.3");Q70=makeQuery(id+"F0.imprint","IMPRINT",FACE,{"disambiguationData":[TD([[makeQuery(id+"F0.imprint","IMPRINT",EDGE,{"derivedFrom":subQ0}),1.0]])]});}
            var Q71;
            {var subQ0=sQuery(id+"F0.wireOp",EDGE,"E25");var subQ1=sQuery(id+"F0.wireOp",EDGE,"E1");var subQ2=makeQuery(id+"F0.imprint","INTERSECT",VERTEX,{"derivedFrom":[subQ1,subQ0]});Q71=makeQuery(id+"F0.imprint","IMPRINT",FACE,{"disambiguationData":[TD([[makeQuery(id+"F0.imprint","IMPRINT",EDGE,{"disambiguationData":[TD([[subQ2,-1.0]])],"derivedFrom":subQ1}),-1.0]])]});}
            var Q72;
            {var subQ1=sQuery(id+"F0.wireOp",EDGE,"E17");var subQ3=sQuery(id+"F0.wireOp",EDGE,"E31");var subQ4=makeQuery(id+"F0.imprint","INTERSECT",VERTEX,{"derivedFrom":[subQ1,subQ3]});Q72=makeQuery(id+"F0.imprint","IMPRINT",FACE,{"disambiguationData":[TD([[makeQuery(id+"F0.imprint","IMPRINT",EDGE,{"disambiguationData":[TD([[subQ4,1.0]])],"derivedFrom":subQ3}),1.0]])]});}
            var Q73;
            {var subQ5=sQuery(id+"F0.wireOp",EDGE,"E31");var subQ6=sQuery(id+"F0.wireOp",EDGE,"E1");var subQ7=makeQuery(id+"F0.imprint","INTERSECT",VERTEX,{"disambiguationData":[OD(0.0)],"derivedFrom":[subQ6,subQ5]});Q73=makeQuery(id+"F0.imprint","IMPRINT",FACE,{"disambiguationData":[TD([[makeQuery(id+"F0.imprint","IMPRINT",EDGE,{"disambiguationData":[TD([[subQ7,-1.0]])],"derivedFrom":subQ6}),-1.0]])]});}
            var Q74;
            {var subQ1=sQuery(id+"F0.wireOp",EDGE,"E11");var subQ3=sQuery(id+"F0.wireOp",EDGE,"E36.4");var subQ4=makeQuery(id+"F0.imprint","INTERSECT",VERTEX,{"derivedFrom":[subQ1,subQ3]});Q74=makeQuery(id+"F0.imprint","IMPRINT",FACE,{"disambiguationData":[TD([[makeQuery(id+"F0.imprint","IMPRINT",EDGE,{"disambiguationData":[TD([[subQ4,-1.0]])],"derivedFrom":subQ1}),1.0]])]});}
            var Q75;
            {var subQ0=sQuery(id+"F0.wireOp",EDGE,"E26");var subQ1=sQuery(id+"F0.wireOp",EDGE,"E25");var subQ2=makeQuery(id+"F0.imprint","INTERSECT",VERTEX,{"derivedFrom":[subQ1,subQ0]});Q75=makeQuery(id+"F0.imprint","IMPRINT",FACE,{"disambiguationData":[TD([[makeQuery(id+"F0.imprint","IMPRINT",EDGE,{"disambiguationData":[TD([[subQ2,1.0]])],"derivedFrom":subQ1}),-1.0]])]});}
            extrude(context, id + "F1", {"entities" : qUnion([Q0, Q1, Q2, Q3, Q4, Q5, Q6, Q7, Q8, Q9, Q10, Q11, Q12, Q13, Q14, Q15, Q16, Q17, Q18, Q19, Q20, Q21, Q22, Q23, Q24, Q25, Q26, Q27, Q28, Q29, Q30, Q31, Q32, Q33, Q34, Q35, Q36, Q37, Q38, Q39, Q40, Q41, Q42, Q43, Q44, Q45, Q46, Q47, Q48, Q49, Q50, Q51, Q52, Q53, Q54, Q55, Q56, Q57, Q58, Q59, Q60, Q61, Q62, Q63, Q64, Q65, Q66, Q67, Q68, Q69, Q70, Q71, Q72, Q73, Q74, Q75]), "depth" : 8 * mm, "offsetDistance" : 25 * mm});
        }
        {
            var Q0;
            Q0=makeQuery(id+"F1.opExtrude","SWEPT_EDGE",EDGE,{"disambiguationData":[OSD([sQuery(id+"F0.wireOp",EDGE,"E25"),sQuery(id+"F0.wireOp",EDGE,"E26")])]});
            var Q1;
            Q1=makeQuery(id+"F1.opExtrude","SWEPT_EDGE",EDGE,{"disambiguationData":[OSD([sQuery(id+"F0.wireOp",EDGE,"E21"),sQuery(id+"F0.wireOp",EDGE,"E22")])]});
            var Q2;
            Q2=makeQuery(id+"F1.opExtrude","SWEPT_EDGE",EDGE,{"disambiguationData":[OSD([sQuery(id+"F0.wireOp",EDGE,"E23"),sQuery(id+"F0.wireOp",EDGE,"E24")])]});
            fillet(context, id + "F2", {"entities" : qUnion([Q0, Q1, Q2]), "radius" : 20 * mm, "tangentPropagation" : true, "allowEdgeOverflow" : false});
        }
        {
            var Q0;
            Q0=makeQuery(id+"F2.opFillet","BLEND_EDGE",EDGE,{"blendedFrom":[makeQuery(id+"F1.opExtrude","SWEPT_EDGE",EDGE,{"disambiguationData":[OSD([sQuery(id+"F0.wireOp",EDGE,"E21"),sQuery(id+"F0.wireOp",EDGE,"E22")])]}),makeQuery(id+"F1.opExtrude","SWEPT_FACE",FACE,{"disambiguationData":[OSD([sQuery(id+"F0.wireOp",EDGE,"E29")])]})],"blendedInto":[makeQuery(id+"F1.opExtrude","SWEPT_FACE",FACE,{"disambiguationData":[OSD([sQuery(id+"F0.wireOp",EDGE,"E29")])]})]});
            var Q1;
            Q1=makeQuery(id+"F2.opFillet","BLEND_EDGE",EDGE,{"blendedFrom":[makeQuery(id+"F1.opExtrude","SWEPT_EDGE",EDGE,{"disambiguationData":[OSD([sQuery(id+"F0.wireOp",EDGE,"E21"),sQuery(id+"F0.wireOp",EDGE,"E22")])]}),makeQuery(id+"F1.opExtrude","SWEPT_FACE",FACE,{"disambiguationData":[OSD([sQuery(id+"F0.wireOp",EDGE,"E27")])]})],"blendedInto":[makeQuery(id+"F1.opExtrude","SWEPT_FACE",FACE,{"disambiguationData":[OSD([sQuery(id+"F0.wireOp",EDGE,"E27")])]})]});
            var Q2;
            Q2=makeQuery(id+"F2.opFillet","BLEND_EDGE",EDGE,{"blendedFrom":[makeQuery(id+"F1.opExtrude","SWEPT_EDGE",EDGE,{"disambiguationData":[OSD([sQuery(id+"F0.wireOp",EDGE,"E23"),sQuery(id+"F0.wireOp",EDGE,"E24")])]}),makeQuery(id+"F1.opExtrude","SWEPT_FACE",FACE,{"disambiguationData":[OSD([sQuery(id+"F0.wireOp",EDGE,"E27")])]})],"blendedInto":[makeQuery(id+"F1.opExtrude","SWEPT_FACE",FACE,{"disambiguationData":[OSD([sQuery(id+"F0.wireOp",EDGE,"E27")])]})]});
            var Q3;
            Q3=makeQuery(id+"F2.opFillet","BLEND_EDGE",EDGE,{"blendedFrom":[makeQuery(id+"F1.opExtrude","SWEPT_EDGE",EDGE,{"disambiguationData":[OSD([sQuery(id+"F0.wireOp",EDGE,"E23"),sQuery(id+"F0.wireOp",EDGE,"E24")])]}),makeQuery(id+"F1.opExtrude","SWEPT_FACE",FACE,{"disambiguationData":[OSD([sQuery(id+"F0.wireOp",EDGE,"E28")])]})],"blendedInto":[makeQuery(id+"F1.opExtrude","SWEPT_FACE",FACE,{"disambiguationData":[OSD([sQuery(id+"F0.wireOp",EDGE,"E28")])]})]});
            var Q4;
            Q4=makeQuery(id+"F2.opFillet","BLEND_EDGE",EDGE,{"blendedFrom":[makeQuery(id+"F1.opExtrude","SWEPT_EDGE",EDGE,{"disambiguationData":[OSD([sQuery(id+"F0.wireOp",EDGE,"E25"),sQuery(id+"F0.wireOp",EDGE,"E26")])]}),makeQuery(id+"F1.opExtrude","SWEPT_FACE",FACE,{"disambiguationData":[OSD([sQuery(id+"F0.wireOp",EDGE,"E28")])]})],"blendedInto":[makeQuery(id+"F1.opExtrude","SWEPT_FACE",FACE,{"disambiguationData":[OSD([sQuery(id+"F0.wireOp",EDGE,"E28")])]})]});
            var Q5;
            Q5=makeQuery(id+"F2.opFillet","BLEND_EDGE",EDGE,{"blendedFrom":[makeQuery(id+"F1.opExtrude","SWEPT_EDGE",EDGE,{"disambiguationData":[OSD([sQuery(id+"F0.wireOp",EDGE,"E25"),sQuery(id+"F0.wireOp",EDGE,"E26")])]}),makeQuery(id+"F1.opExtrude","SWEPT_FACE",FACE,{"disambiguationData":[OSD([sQuery(id+"F0.wireOp",EDGE,"E29")])]})],"blendedInto":[makeQuery(id+"F1.opExtrude","SWEPT_FACE",FACE,{"disambiguationData":[OSD([sQuery(id+"F0.wireOp",EDGE,"E29")])]})]});
            fillet(context, id + "F3", {"entities" : qUnion([Q0, Q1, Q2, Q3, Q4, Q5]), "radius" : 5 * mm, "tangentPropagation" : true, "allowEdgeOverflow" : false});
        }
        {
            var Q0;
            Q0=makeQuery(id+"F1.opExtrude","CAP_EDGE",EDGE,{"disambiguationData":[OSD([sQuery(id+"F0.wireOp",EDGE,"E34.0")])],"isStart":false});
            var Q1;
            Q1=makeQuery(id+"F1.opExtrude","CAP_EDGE",EDGE,{"disambiguationData":[OSD([sQuery(id+"F0.wireOp",EDGE,"E34.1")])],"isStart":false});
            var Q2;
            Q2=makeQuery(id+"F1.opExtrude","CAP_EDGE",EDGE,{"disambiguationData":[OSD([sQuery(id+"F0.wireOp",EDGE,"E34.2")])],"isStart":false});
            var Q3;
            Q3=makeQuery(id+"F1.opExtrude","CAP_EDGE",EDGE,{"disambiguationData":[OSD([sQuery(id+"F0.wireOp",EDGE,"E34.3")])],"isStart":false});
            var Q4;
            Q4=makeQuery(id+"F1.opExtrude","CAP_EDGE",EDGE,{"disambiguationData":[OSD([sQuery(id+"F0.wireOp",EDGE,"E34.4")])],"isStart":false});
            var Q5;
            Q5=makeQuery(id+"F1.opExtrude","CAP_EDGE",EDGE,{"disambiguationData":[OSD([sQuery(id+"F0.wireOp",EDGE,"E34.5")])],"isStart":false});
            var Q6;
            Q6=makeQuery(id+"F1.opExtrude","CAP_EDGE",EDGE,{"disambiguationData":[OSD([sQuery(id+"F0.wireOp",EDGE,"E35.1")])],"isStart":false});
            var Q7;
            Q7=makeQuery(id+"F1.opExtrude","CAP_EDGE",EDGE,{"disambiguationData":[OSD([sQuery(id+"F0.wireOp",EDGE,"E35.2")])],"isStart":false});
            var Q8;
            Q8=makeQuery(id+"F1.opExtrude","CAP_EDGE",EDGE,{"disambiguationData":[OSD([sQuery(id+"F0.wireOp",EDGE,"E35.3")])],"isStart":false});
            var Q9;
            Q9=makeQuery(id+"F1.opExtrude","CAP_EDGE",EDGE,{"disambiguationData":[OSD([sQuery(id+"F0.wireOp",EDGE,"E35.4")])],"isStart":false});
            var Q10;
            Q10=makeQuery(id+"F1.opExtrude","CAP_EDGE",EDGE,{"disambiguationData":[OSD([sQuery(id+"F0.wireOp",EDGE,"E35.5")])],"isStart":false});
            var Q11;
            Q11=makeQuery(id+"F1.opExtrude","CAP_EDGE",EDGE,{"disambiguationData":[OSD([sQuery(id+"F0.wireOp",EDGE,"E35.0")])],"isStart":false});
            var Q12;
            Q12=makeQuery(id+"F1.opExtrude","CAP_EDGE",EDGE,{"disambiguationData":[OSD([sQuery(id+"F0.wireOp",EDGE,"E36.1")])],"isStart":false});
            var Q13;
            Q13=makeQuery(id+"F1.opExtrude","CAP_EDGE",EDGE,{"disambiguationData":[OSD([sQuery(id+"F0.wireOp",EDGE,"E36.2")])],"isStart":false});
            var Q14;
            Q14=makeQuery(id+"F1.opExtrude","CAP_EDGE",EDGE,{"disambiguationData":[OSD([sQuery(id+"F0.wireOp",EDGE,"E36.3")])],"isStart":false});
            var Q15;
            Q15=makeQuery(id+"F1.opExtrude","CAP_EDGE",EDGE,{"disambiguationData":[OSD([sQuery(id+"F0.wireOp",EDGE,"E36.4")])],"isStart":false});
            var Q16;
            Q16=makeQuery(id+"F1.opExtrude","CAP_EDGE",EDGE,{"disambiguationData":[OSD([sQuery(id+"F0.wireOp",EDGE,"E36.5")])],"isStart":false});
            var Q17;
            Q17=makeQuery(id+"F1.opExtrude","CAP_EDGE",EDGE,{"disambiguationData":[OSD([sQuery(id+"F0.wireOp",EDGE,"E36.0")])],"isStart":false});
            var Q18;
            Q18=makeQuery(id+"F1.opExtrude","CAP_EDGE",EDGE,{"disambiguationData":[OSD([sQuery(id+"F0.wireOp",EDGE,"E36.3")])],"isStart":true});
            var Q19;
            Q19=makeQuery(id+"F1.opExtrude","CAP_EDGE",EDGE,{"disambiguationData":[OSD([sQuery(id+"F0.wireOp",EDGE,"E36.2")])],"isStart":true});
            var Q20;
            Q20=makeQuery(id+"F1.opExtrude","SWEPT_FACE",FACE,{"disambiguationData":[OSD([sQuery(id+"F0.wireOp",EDGE,"E36.4")])]});
            var Q21;
            Q21=makeQuery(id+"F1.opExtrude","CAP_EDGE",EDGE,{"disambiguationData":[OSD([sQuery(id+"F0.wireOp",EDGE,"E34.3")])],"isStart":true});
            var Q22;
            Q22=makeQuery(id+"F1.opExtrude","CAP_EDGE",EDGE,{"disambiguationData":[OSD([sQuery(id+"F0.wireOp",EDGE,"E34.4")])],"isStart":true});
            var Q23;
            Q23=makeQuery(id+"F1.opExtrude","CAP_EDGE",EDGE,{"disambiguationData":[OSD([sQuery(id+"F0.wireOp",EDGE,"E34.2")])],"isStart":true});
            var Q24;
            Q24=makeQuery(id+"F1.opExtrude","CAP_EDGE",EDGE,{"disambiguationData":[OSD([sQuery(id+"F0.wireOp",EDGE,"E34.5")])],"isStart":true});
            var Q25;
            Q25=makeQuery(id+"F1.opExtrude","CAP_EDGE",EDGE,{"disambiguationData":[OSD([sQuery(id+"F0.wireOp",EDGE,"E36.1")])],"isStart":true});
            var Q26;
            Q26=makeQuery(id+"F1.opExtrude","CAP_EDGE",EDGE,{"disambiguationData":[OSD([sQuery(id+"F0.wireOp",EDGE,"E36.0")])],"isStart":true});
            var Q27;
            Q27=makeQuery(id+"F1.opExtrude","CAP_EDGE",EDGE,{"disambiguationData":[OSD([sQuery(id+"F0.wireOp",EDGE,"E34.1")])],"isStart":true});
            var Q28;
            Q28=makeQuery(id+"F1.opExtrude","CAP_EDGE",EDGE,{"disambiguationData":[OSD([sQuery(id+"F0.wireOp",EDGE,"E34.0")])],"isStart":true});
            var Q29;
            Q29=makeQuery(id+"F1.opExtrude","CAP_EDGE",EDGE,{"disambiguationData":[OSD([sQuery(id+"F0.wireOp",EDGE,"E35.2")])],"isStart":true});
            var Q30;
            Q30=makeQuery(id+"F1.opExtrude","CAP_EDGE",EDGE,{"disambiguationData":[OSD([sQuery(id+"F0.wireOp",EDGE,"E35.1")])],"isStart":true});
            var Q31;
            Q31=makeQuery(id+"F1.opExtrude","CAP_EDGE",EDGE,{"disambiguationData":[OSD([sQuery(id+"F0.wireOp",EDGE,"E30")])],"isStart":true});
            var Q32;
            Q32=makeQuery(id+"F1.opExtrude","CAP_EDGE",EDGE,{"disambiguationData":[OSD([sQuery(id+"F0.wireOp",EDGE,"E30")])],"isStart":false});
            var Q33;
            Q33=makeQuery(id+"F1.opExtrude","CAP_EDGE",EDGE,{"disambiguationData":[OSD([sQuery(id+"F0.wireOp",EDGE,"E35.3")])],"isStart":true});
            var Q34;
            Q34=makeQuery(id+"F1.opExtrude","CAP_EDGE",EDGE,{"disambiguationData":[OSD([sQuery(id+"F0.wireOp",EDGE,"E35.0")])],"isStart":true});
            var Q35;
            Q35=makeQuery(id+"F1.opExtrude","CAP_EDGE",EDGE,{"disambiguationData":[OSD([sQuery(id+"F0.wireOp",EDGE,"E35.5")])],"isStart":true});
            var Q36;
            Q36=makeQuery(id+"F1.opExtrude","CAP_EDGE",EDGE,{"disambiguationData":[OSD([sQuery(id+"F0.wireOp",EDGE,"E35.4")])],"isStart":true});
            chamfer(context, id + "F4", {"entities" : qUnion([Q0, Q1, Q2, Q3, Q4, Q5, Q6, Q7, Q8, Q9, Q10, Q11, Q12, Q13, Q14, Q15, Q16, Q17, Q18, Q19, Q20, Q21, Q22, Q23, Q24, Q25, Q26, Q27, Q28, Q29, Q30, Q31, Q32, Q33, Q34, Q35, Q36]), "width" : 1 * mm, "tangentPropagation" : true});
        }
        {
            var Q0;
            {var subQ0=sQuery(id+"F0.wireOp",EDGE,"E26");var subQ1=sQuery(id+"F0.wireOp",EDGE,"E25");Q0=makeQuery(id+"F2.opFillet","BLEND_EDGE",EDGE,{"blendedFrom":[makeQuery(id+"F1.opExtrude","SWEPT_EDGE",EDGE,{"disambiguationData":[OSD([subQ1,subQ0])]}),makeQuery(id+"F1.opExtrude","CAP_FACE",FACE,{"disambiguationData":[OSD([sQuery(id+"F0.wireOp",EDGE,"E1"),sQuery(id+"F0.wireOp",EDGE,"E21"),sQuery(id+"F0.wireOp",EDGE,"E22"),sQuery(id+"F0.wireOp",EDGE,"E23"),sQuery(id+"F0.wireOp",EDGE,"E24"),subQ1,subQ0,sQuery(id+"F0.wireOp",EDGE,"E27"),sQuery(id+"F0.wireOp",EDGE,"E28"),sQuery(id+"F0.wireOp",EDGE,"E29"),sQuery(id+"F0.wireOp",EDGE,"E30"),sQuery(id+"F0.wireOp",EDGE,"E33"),sQuery(id+"F0.wireOp",EDGE,"E34.0"),sQuery(id+"F0.wireOp",EDGE,"E34.1"),sQuery(id+"F0.wireOp",EDGE,"E34.2"),sQuery(id+"F0.wireOp",EDGE,"E34.3"),sQuery(id+"F0.wireOp",EDGE,"E34.4"),sQuery(id+"F0.wireOp",EDGE,"E34.5"),sQuery(id+"F0.wireOp",EDGE,"E35.0"),sQuery(id+"F0.wireOp",EDGE,"E35.1"),sQuery(id+"F0.wireOp",EDGE,"E35.2"),sQuery(id+"F0.wireOp",EDGE,"E35.3"),sQuery(id+"F0.wireOp",EDGE,"E35.4"),sQuery(id+"F0.wireOp",EDGE,"E35.5"),sQuery(id+"F0.wireOp",EDGE,"E36.0"),sQuery(id+"F0.wireOp",EDGE,"E36.1"),sQuery(id+"F0.wireOp",EDGE,"E36.2"),sQuery(id+"F0.wireOp",EDGE,"E36.3"),sQuery(id+"F0.wireOp",EDGE,"E36.4"),sQuery(id+"F0.wireOp",EDGE,"E36.5")])],"isStart":true})],"blendedInto":[makeQuery(id+"F1.opExtrude","CAP_FACE",FACE,{"disambiguationData":[OSD([sQuery(id+"F0.wireOp",EDGE,"E1"),sQuery(id+"F0.wireOp",EDGE,"E21"),sQuery(id+"F0.wireOp",EDGE,"E22"),sQuery(id+"F0.wireOp",EDGE,"E23"),sQuery(id+"F0.wireOp",EDGE,"E24"),subQ1,subQ0,sQuery(id+"F0.wireOp",EDGE,"E27"),sQuery(id+"F0.wireOp",EDGE,"E28"),sQuery(id+"F0.wireOp",EDGE,"E29"),sQuery(id+"F0.wireOp",EDGE,"E30"),sQuery(id+"F0.wireOp",EDGE,"E33"),sQuery(id+"F0.wireOp",EDGE,"E34.0"),sQuery(id+"F0.wireOp",EDGE,"E34.1"),sQuery(id+"F0.wireOp",EDGE,"E34.2"),sQuery(id+"F0.wireOp",EDGE,"E34.3"),sQuery(id+"F0.wireOp",EDGE,"E34.4"),sQuery(id+"F0.wireOp",EDGE,"E34.5"),sQuery(id+"F0.wireOp",EDGE,"E35.0"),sQuery(id+"F0.wireOp",EDGE,"E35.1"),sQuery(id+"F0.wireOp",EDGE,"E35.2"),sQuery(id+"F0.wireOp",EDGE,"E35.3"),sQuery(id+"F0.wireOp",EDGE,"E35.4"),sQuery(id+"F0.wireOp",EDGE,"E35.5"),sQuery(id+"F0.wireOp",EDGE,"E36.0"),sQuery(id+"F0.wireOp",EDGE,"E36.1"),sQuery(id+"F0.wireOp",EDGE,"E36.2"),sQuery(id+"F0.wireOp",EDGE,"E36.3"),sQuery(id+"F0.wireOp",EDGE,"E36.4"),sQuery(id+"F0.wireOp",EDGE,"E36.5")])],"isStart":true})]});}
            var Q1;
            {var subQ0=sQuery(id+"F0.wireOp",EDGE,"E22");var subQ1=sQuery(id+"F0.wireOp",EDGE,"E21");Q1=makeQuery(id+"F2.opFillet","BLEND_EDGE",EDGE,{"blendedFrom":[makeQuery(id+"F1.opExtrude","SWEPT_EDGE",EDGE,{"disambiguationData":[OSD([subQ1,subQ0])]}),makeQuery(id+"F1.opExtrude","CAP_FACE",FACE,{"disambiguationData":[OSD([sQuery(id+"F0.wireOp",EDGE,"E1"),subQ1,subQ0,sQuery(id+"F0.wireOp",EDGE,"E23"),sQuery(id+"F0.wireOp",EDGE,"E24"),sQuery(id+"F0.wireOp",EDGE,"E25"),sQuery(id+"F0.wireOp",EDGE,"E26"),sQuery(id+"F0.wireOp",EDGE,"E27"),sQuery(id+"F0.wireOp",EDGE,"E28"),sQuery(id+"F0.wireOp",EDGE,"E29"),sQuery(id+"F0.wireOp",EDGE,"E30"),sQuery(id+"F0.wireOp",EDGE,"E33"),sQuery(id+"F0.wireOp",EDGE,"E34.0"),sQuery(id+"F0.wireOp",EDGE,"E34.1"),sQuery(id+"F0.wireOp",EDGE,"E34.2"),sQuery(id+"F0.wireOp",EDGE,"E34.3"),sQuery(id+"F0.wireOp",EDGE,"E34.4"),sQuery(id+"F0.wireOp",EDGE,"E34.5"),sQuery(id+"F0.wireOp",EDGE,"E35.0"),sQuery(id+"F0.wireOp",EDGE,"E35.1"),sQuery(id+"F0.wireOp",EDGE,"E35.2"),sQuery(id+"F0.wireOp",EDGE,"E35.3"),sQuery(id+"F0.wireOp",EDGE,"E35.4"),sQuery(id+"F0.wireOp",EDGE,"E35.5"),sQuery(id+"F0.wireOp",EDGE,"E36.0"),sQuery(id+"F0.wireOp",EDGE,"E36.1"),sQuery(id+"F0.wireOp",EDGE,"E36.2"),sQuery(id+"F0.wireOp",EDGE,"E36.3"),sQuery(id+"F0.wireOp",EDGE,"E36.4"),sQuery(id+"F0.wireOp",EDGE,"E36.5")])],"isStart":false})],"blendedInto":[makeQuery(id+"F1.opExtrude","CAP_FACE",FACE,{"disambiguationData":[OSD([sQuery(id+"F0.wireOp",EDGE,"E1"),subQ1,subQ0,sQuery(id+"F0.wireOp",EDGE,"E23"),sQuery(id+"F0.wireOp",EDGE,"E24"),sQuery(id+"F0.wireOp",EDGE,"E25"),sQuery(id+"F0.wireOp",EDGE,"E26"),sQuery(id+"F0.wireOp",EDGE,"E27"),sQuery(id+"F0.wireOp",EDGE,"E28"),sQuery(id+"F0.wireOp",EDGE,"E29"),sQuery(id+"F0.wireOp",EDGE,"E30"),sQuery(id+"F0.wireOp",EDGE,"E33"),sQuery(id+"F0.wireOp",EDGE,"E34.0"),sQuery(id+"F0.wireOp",EDGE,"E34.1"),sQuery(id+"F0.wireOp",EDGE,"E34.2"),sQuery(id+"F0.wireOp",EDGE,"E34.3"),sQuery(id+"F0.wireOp",EDGE,"E34.4"),sQuery(id+"F0.wireOp",EDGE,"E34.5"),sQuery(id+"F0.wireOp",EDGE,"E35.0"),sQuery(id+"F0.wireOp",EDGE,"E35.1"),sQuery(id+"F0.wireOp",EDGE,"E35.2"),sQuery(id+"F0.wireOp",EDGE,"E35.3"),sQuery(id+"F0.wireOp",EDGE,"E35.4"),sQuery(id+"F0.wireOp",EDGE,"E35.5"),sQuery(id+"F0.wireOp",EDGE,"E36.0"),sQuery(id+"F0.wireOp",EDGE,"E36.1"),sQuery(id+"F0.wireOp",EDGE,"E36.2"),sQuery(id+"F0.wireOp",EDGE,"E36.3"),sQuery(id+"F0.wireOp",EDGE,"E36.4"),sQuery(id+"F0.wireOp",EDGE,"E36.5")])],"isStart":false})]});}
            fillet(context, id + "F5", {"entities" : qUnion([Q0, Q1]), "radius" : 3 * mm, "tangentPropagation" : true, "allowEdgeOverflow" : false});
        }
    });
